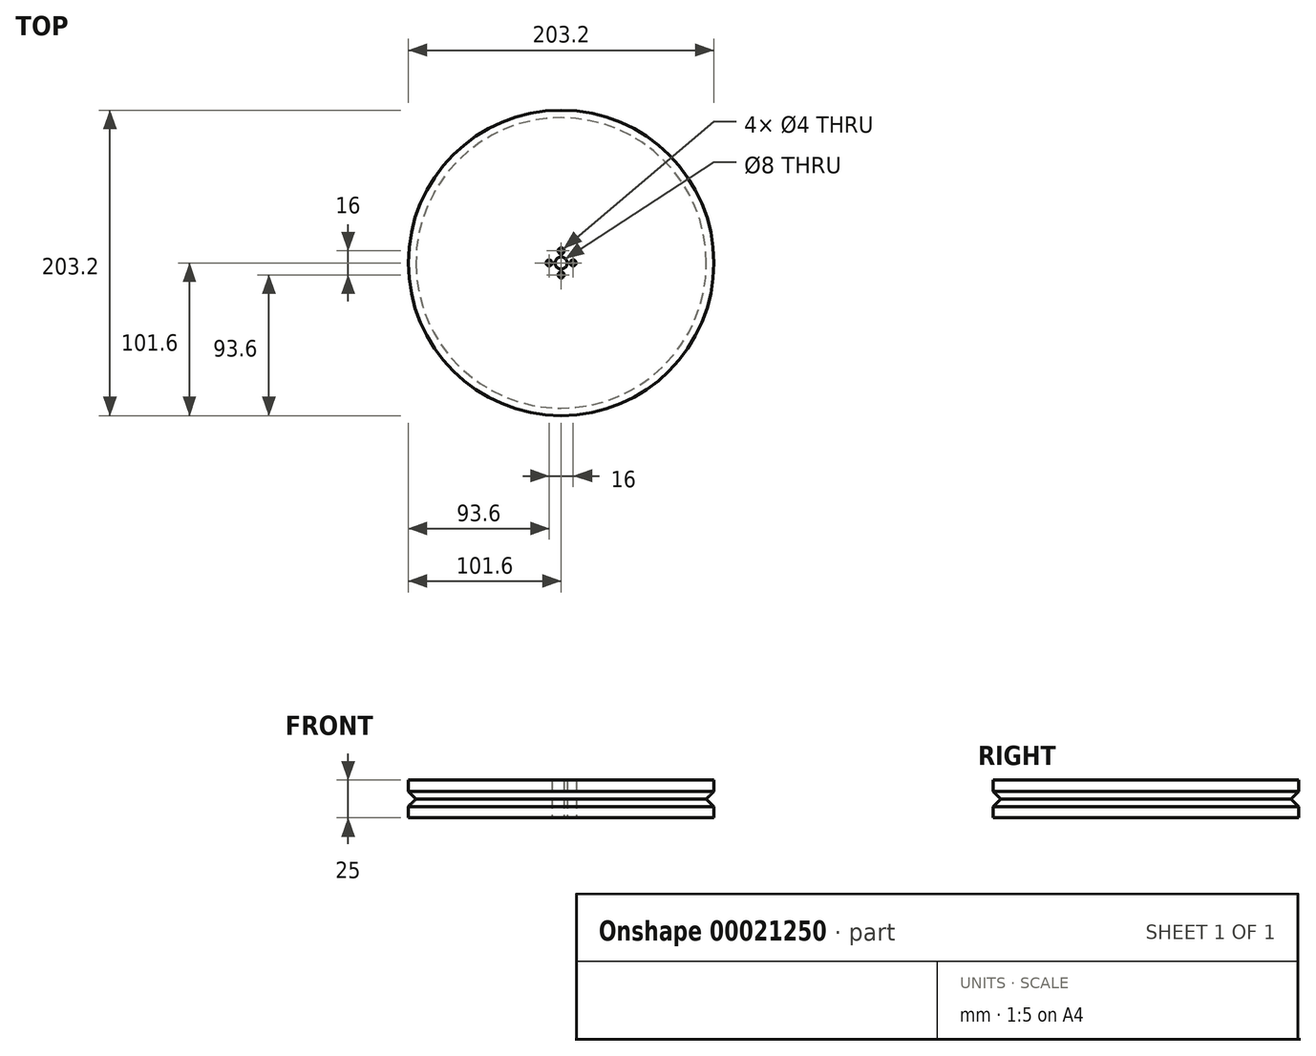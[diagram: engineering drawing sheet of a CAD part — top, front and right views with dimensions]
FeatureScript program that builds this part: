
annotation { "Feature Type Name" : "Feature", "Feature Type Description" : "" }
export const myFeature = defineFeature(function(context is Context, id is Id, definition is map)
    precondition{}
    {
        {
            var Q0;
            Q0=qCreatedBy(makeId("Top.planeOp"),FACE);
            var sketch = newSketch(context, id + "F0", { "sketchPlane" : qUnion([Q0])});
            skCircle(sketch, "E0", {"center": v(0, 0) * mm, "radius": 4 * mm});
            skCircle(sketch, "E1", {"center": v(8, 0) * mm, "radius": 2 * mm});
            skCircle(sketch, "E2.1.0", {"center": v(0, 8) * mm, "radius": 2 * mm});
            skCircle(sketch, "E2.2.0", {"center": v(-8, 0) * mm, "radius": 2 * mm});
            skCircle(sketch, "E2.3.0", {"center": v(0, -8) * mm, "radius": 2 * mm});
            skCircle(sketch, "E3", {"center": v(0, 0) * mm, "radius": 12 * mm});
            skCircle(sketch, "E4", {"center": v(0, 0) * mm, "radius": 101.6 * mm});
            skCircle(sketch, "E5", {"center": v(0, 0) * mm, "radius": 96.6 * mm});
            skSolve(sketch);
        }
        {
            var Q0;
            Q0=makeQuery(id+"F0.imprint","IMPRINT",FACE,{"disambiguationData":[TD([[makeQuery(id+"F0.imprint","IMPRINT",EDGE,{"derivedFrom":sQuery(id+"F0.wireOp",EDGE,"E3")}),-1.0]])]});
            var Q1;
            Q1=makeQuery(id+"F0.imprint","IMPRINT",FACE,{"disambiguationData":[TD([[makeQuery(id+"F0.imprint","IMPRINT",EDGE,{"derivedFrom":sQuery(id+"F0.wireOp",EDGE,"E0")}),-1.0]])]});
            extrude(context, id + "F1", {"entities" : qUnion([Q0, Q1]), "endBound" : BoundingType.SYMMETRIC, "depth" : 25 * mm});
        }
        {
            var Q0;
            Q0=makeQuery(id+"F0.imprint","IMPRINT",FACE,{"disambiguationData":[TD([[makeQuery(id+"F0.imprint","IMPRINT",EDGE,{"derivedFrom":sQuery(id+"F0.wireOp",EDGE,"E4")}),1.0]])]});
            extrude(context, id + "F2", {"entities" : qUnion([Q0]), "operationType" : NewBodyOperationType.ADD, "endBound" : BoundingType.SYMMETRIC, "depth" : 25 * mm});
        }
        {
            var Q0;
            Q0=makeQuery(id+"F0.imprint","IMPRINT",FACE,{"disambiguationData":[TD([[makeQuery(id+"F0.imprint","IMPRINT",EDGE,{"derivedFrom":sQuery(id+"F0.wireOp",EDGE,"E4")}),1.0]])]});
            extrude(context, id + "F3", {"entities" : qUnion([Q0]), "operationType" : NewBodyOperationType.REMOVE, "endBound" : BoundingType.SYMMETRIC, "oppositeDirection" : true, "depth" : 20 * mm});
        }
        {
            var Q0;
            Q0=makeQuery(id+"F3.boolean.opBoolean","COPY",EDGE,{"derivedFrom":makeQuery(id+"F3.opExtrude","CAP_EDGE",EDGE,{"disambiguationData":[OSD([sQuery(id+"F0.wireOp",EDGE,"E5")])],"isStart":false})});
            var Q1;
            Q1=makeQuery(id+"F3.boolean.opBoolean","COPY",EDGE,{"derivedFrom":makeQuery(id+"F3.opExtrude","CAP_EDGE",EDGE,{"disambiguationData":[OSD([sQuery(id+"F0.wireOp",EDGE,"E5")])],"isStart":true})});
            chamfer(context, id + "F4", {"entities" : qUnion([Q0, Q1]), "width" : 10 * mm, "tangentPropagation" : true});
        }
    });
